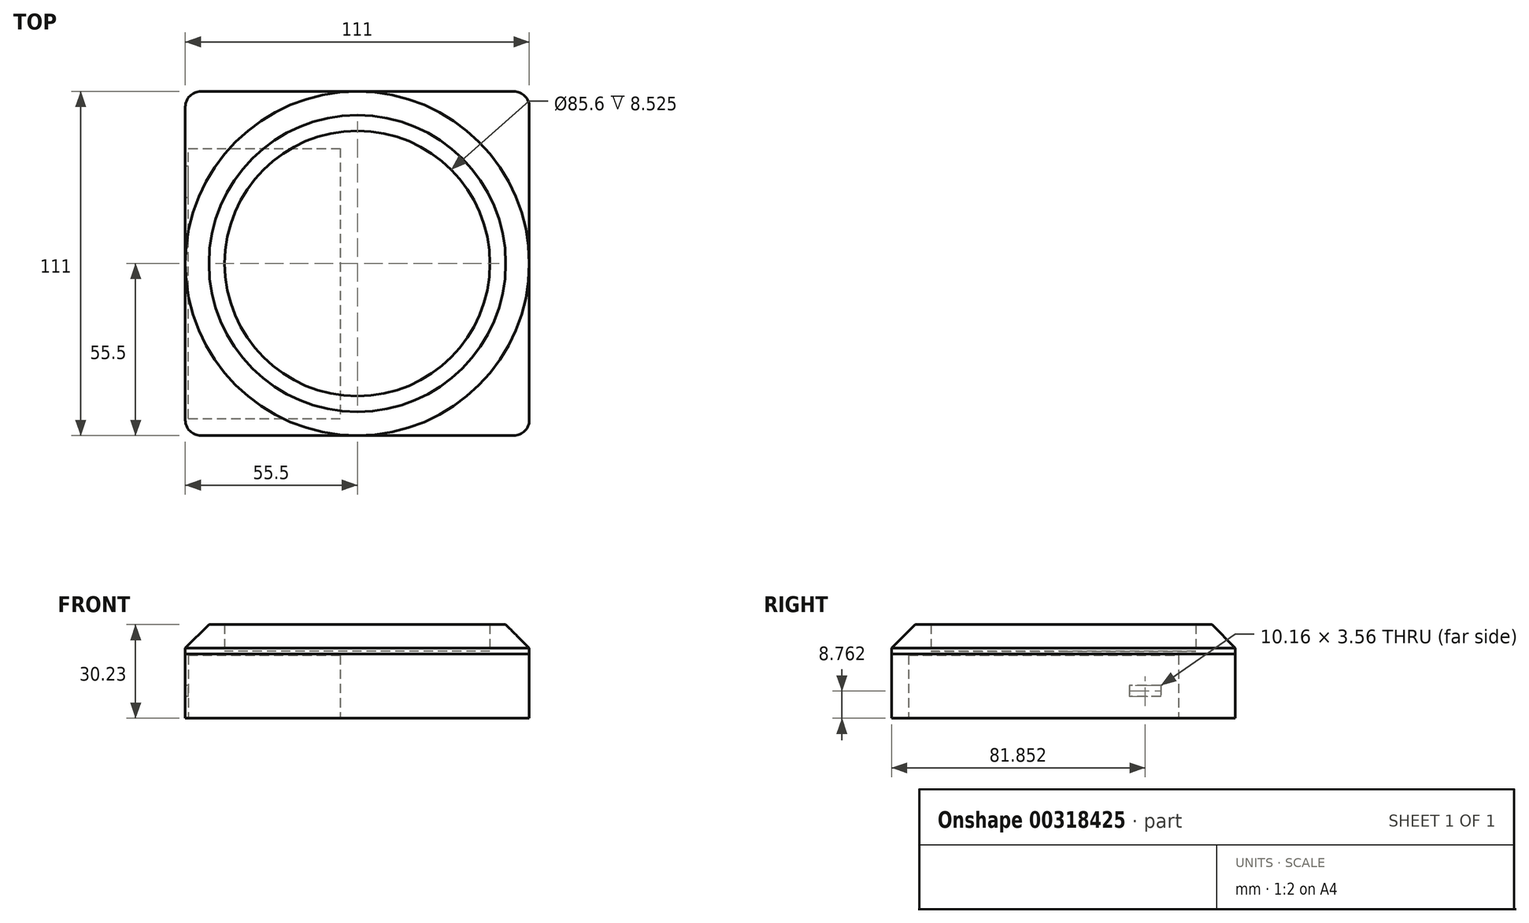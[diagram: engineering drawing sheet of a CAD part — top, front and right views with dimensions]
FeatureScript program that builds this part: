
annotation { "Feature Type Name" : "Feature", "Feature Type Description" : "" }
export const myFeature = defineFeature(function(context is Context, id is Id, definition is map)
    precondition{}
    {
        {
            var Q0;
            Q0=qCreatedBy(makeId("Top.planeOp"),FACE);
            var sketch = newSketch(context, id + "F0", { "sketchPlane" : qUnion([Q0])});
            skCircle(sketch, "E0", {"center": v(0, 0) * mm, "radius": 42.8 * mm});
            skCircle(sketch, "E1", {"center": v(0, 0) * mm, "radius": 1.27 * mm});
            skCircle(sketch, "E2", {"center": v(0, 0) * mm, "radius": 55.5 * mm});
            skSolve(sketch);
        }
        {
            var Q0;
            Q0 = qSketchRegion(id + "F0", true);
            extrude(context, id + "F1", {"entities" : qUnion([Q0]), "depth" : 9.52 * mm});
        }
        {
            var Q0;
            Q0=makeQuery(id+"F1.opExtrude","CAP_FACE",FACE,{"disambiguationData":[OSD([sQuery(id+"F0.wireOp",EDGE,"E0"),sQuery(id+"F0.wireOp",EDGE,"E2")])],"isStart":true});
            var sketch = newSketch(context, id + "F2", { "sketchPlane" : qUnion([Q0])});
            skLineSegment(sketch, "E3.bottom", {"start": v(55.5, -55.5) * mm, "end": v(-55.5, -55.5) * mm});
            skLineSegment(sketch, "E3.top", {"start": v(55.5, 55.5) * mm, "end": v(-55.5, 55.5) * mm});
            skLineSegment(sketch, "E3.left", {"start": v(55.5, -55.5) * mm, "end": v(55.5, 55.5) * mm});
            skLineSegment(sketch, "E3.right", {"start": v(-55.5, -55.5) * mm, "end": v(-55.5, 55.5) * mm});
            skPoint(sketch, "E3.middle", {"position": v(0, 0) * mm});
            skSolve(sketch);
        }
        {
            var Q0;
            Q0 = qSketchRegion(id + "F2", true);
            extrude(context, id + "F3", {"entities" : qUnion([Q0]), "operationType" : NewBodyOperationType.ADD, "depth" : 20.7 * mm});
        }
        {
            var Q0;
            Q0=makeQuery(id+"F1.opExtrude","CAP_EDGE",EDGE,{"disambiguationData":[OSD([sQuery(id+"F0.wireOp",EDGE,"E2")])],"isStart":false});
            chamfer(context, id + "F4", {"entities" : qUnion([Q0]), "width" : 7.62 * mm, "tangentPropagation" : true});
        }
        {
            var Q0;
            Q0=makeQuery(id+"F3.opExtrude","CAP_FACE",FACE,{"disambiguationData":[OSD([sQuery(id+"F2.wireOp",EDGE,"E3.bottom"),sQuery(id+"F2.wireOp",EDGE,"E3.top"),sQuery(id+"F2.wireOp",EDGE,"E3.left"),sQuery(id+"F2.wireOp",EDGE,"E3.right")])],"isStart":false});
            var sketch = newSketch(context, id + "F5", { "sketchPlane" : qUnion([Q0])});
            skLineSegment(sketch, "E4.bottom", {"start": v(-55.5, -37.15) * mm, "end": v(-5.48, -37.15) * mm});
            skLineSegment(sketch, "E4.top", {"start": v(-55.5, 49.97) * mm, "end": v(-5.48, 49.97) * mm});
            skLineSegment(sketch, "E4.left", {"start": v(-55.5, -37.15) * mm, "end": v(-55.5, 49.97) * mm});
            skLineSegment(sketch, "E4.right", {"start": v(-5.48, -37.15) * mm, "end": v(-5.48, 49.97) * mm});
            skLineSegment(sketch, "E5", {"start": v(-54.5, 49.97) * mm, "end": v(-54.5, -37.15) * mm});
            skSolve(sketch);
        }
        {
            var Q0;
            {var subQ0=sQuery(id+"F5.wireOp",EDGE,"E4.right");Q0=makeQuery(id+"F5.imprint","IMPRINT",FACE,{"disambiguationData":[TD([[makeQuery(id+"F5.imprint","IMPRINT",EDGE,{"derivedFrom":subQ0}),1.0]])]});}
            extrude(context, id + "F6", {"entities" : qUnion([Q0]), "operationType" : NewBodyOperationType.REMOVE, "oppositeDirection" : true, "depth" : 20.32 * mm});
        }
        {
            var Q0;
            Q0=makeQuery(id+"F3.opExtrude","SWEPT_FACE",FACE,{"disambiguationData":[OSD([sQuery(id+"F2.wireOp",EDGE,"E3.right")])]});
            var sketch = newSketch(context, id + "F7", { "sketchPlane" : qUnion([Q0])});
            skLineSegment(sketch, "E6.bottom", {"start": v(-31.43, -10.16) * mm, "end": v(-21.27, -10.16) * mm});
            skLineSegment(sketch, "E6.top", {"start": v(-31.43, -13.72) * mm, "end": v(-21.27, -13.72) * mm});
            skLineSegment(sketch, "E6.left", {"start": v(-31.43, -10.16) * mm, "end": v(-31.43, -13.72) * mm});
            skLineSegment(sketch, "E6.right", {"start": v(-21.27, -10.16) * mm, "end": v(-21.27, -13.72) * mm});
            skSolve(sketch);
        }
        {
            var Q0;
            Q0 = qSketchRegion(id + "F7", true);
            extrude(context, id + "F8", {"entities" : qUnion([Q0]), "operationType" : NewBodyOperationType.REMOVE, "endBound" : BoundingType.UP_TO_NEXT, "oppositeDirection" : true, "depth" : 25 * mm});
        }
        {
            var Q0;
            Q0=makeQuery(id+"F3.opExtrude","SWEPT_EDGE",EDGE,{"disambiguationData":[OSD([sQuery(id+"F2.wireOp",EDGE,"E3.top"),sQuery(id+"F2.wireOp",EDGE,"E3.right")])]});
            var Q1;
            Q1=makeQuery(id+"F3.opExtrude","SWEPT_EDGE",EDGE,{"disambiguationData":[OSD([sQuery(id+"F2.wireOp",EDGE,"E3.bottom"),sQuery(id+"F2.wireOp",EDGE,"E3.right")])]});
            var Q2;
            Q2=makeQuery(id+"F3.opExtrude","SWEPT_EDGE",EDGE,{"disambiguationData":[OSD([sQuery(id+"F2.wireOp",EDGE,"E3.top"),sQuery(id+"F2.wireOp",EDGE,"E3.left")])]});
            var Q3;
            Q3=makeQuery(id+"F3.opExtrude","SWEPT_EDGE",EDGE,{"disambiguationData":[OSD([sQuery(id+"F2.wireOp",EDGE,"E3.bottom"),sQuery(id+"F2.wireOp",EDGE,"E3.left")])]});
            fillet(context, id + "F9", {"entities" : qUnion([Q0, Q1, Q2, Q3]), "radius" : 5 * mm, "tangentPropagation" : true, "allowEdgeOverflow" : false});
        }
        {
            var Q0;
            Q0=makeQuery(id+"F3.boolean.opBoolean","SPLIT",FACE,{"disambiguationData":[TD([makeQuery(id+"F1.opExtrude","SWEPT_FACE",FACE,{"disambiguationData":[OSD([sQuery(id+"F0.wireOp",EDGE,"E0")])]})])],"derivedFrom":makeQuery(id+"F3.opExtrude","CAP_FACE",FACE,{"disambiguationData":[OSD([sQuery(id+"F2.wireOp",EDGE,"E3.bottom"),sQuery(id+"F2.wireOp",EDGE,"E3.top"),sQuery(id+"F2.wireOp",EDGE,"E3.left"),sQuery(id+"F2.wireOp",EDGE,"E3.right")])],"isStart":true})});
            var sketch = newSketch(context, id + "F10", { "sketchPlane" : qUnion([Q0])});
            skCircle(sketch, "E7", {"center": v(0, 0) * mm, "radius": 42.8 * mm});
            skSolve(sketch);
        }
        {
            var Q0;
            Q0 = qSketchRegion(id + "F10", true);
            extrude(context, id + "F11", {"entities" : qUnion([Q0]), "operationType" : NewBodyOperationType.ADD, "depth" : 1 * mm});
        }
    });
